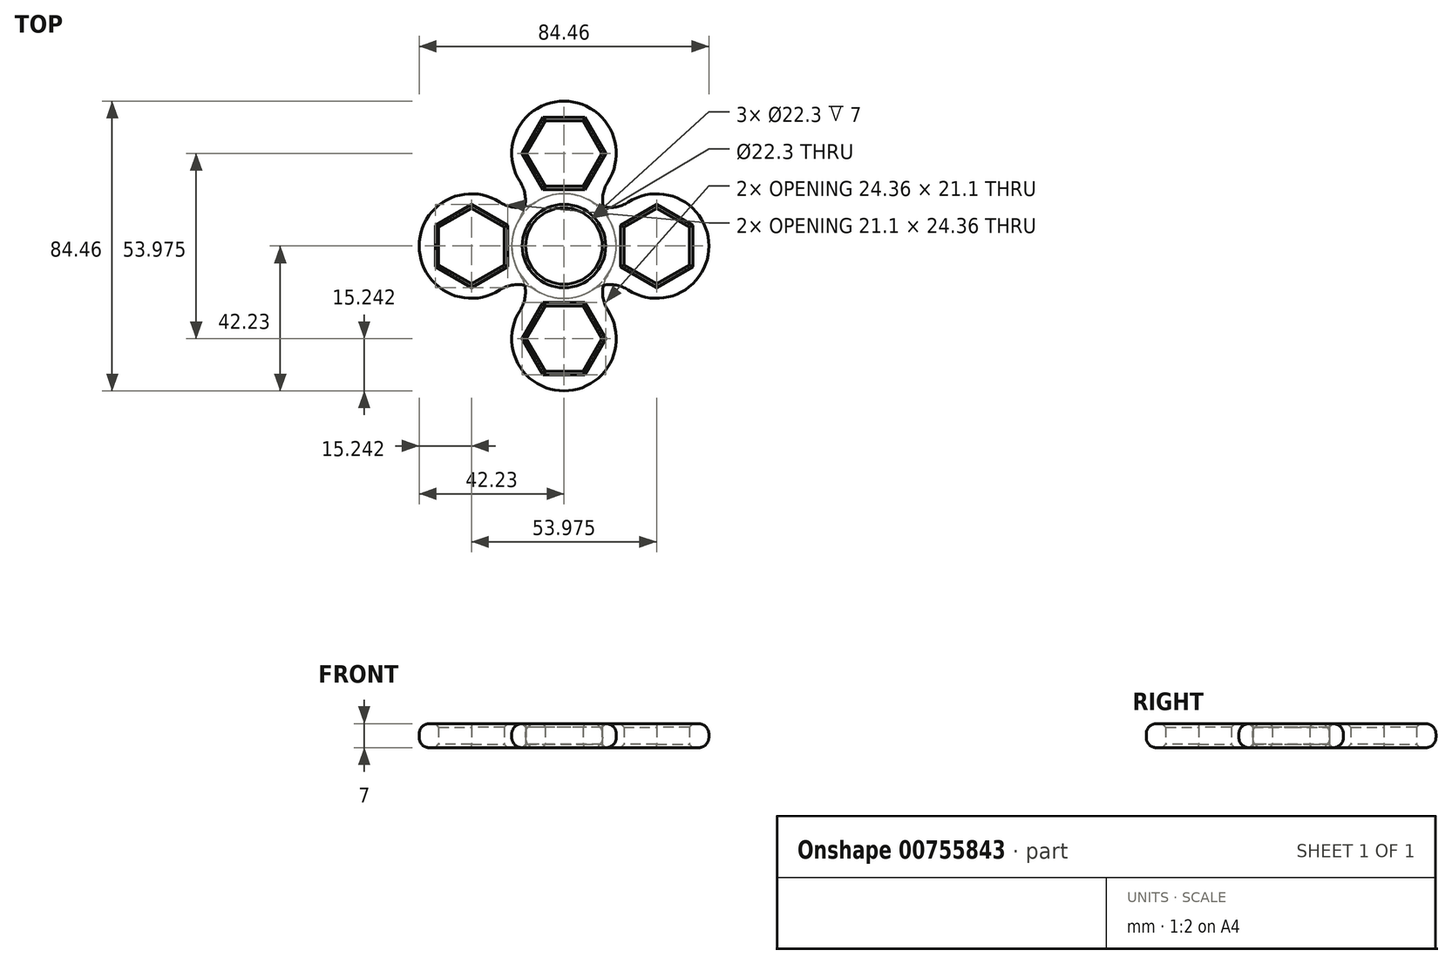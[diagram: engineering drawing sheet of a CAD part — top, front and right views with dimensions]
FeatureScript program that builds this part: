
annotation { "Feature Type Name" : "Feature", "Feature Type Description" : "" }
export const myFeature = defineFeature(function(context is Context, id is Id, definition is map)
    precondition{}
    {
        {
            var Q0;
            Q0=qCreatedBy(makeId("Top.planeOp"),FACE);
            var sketch = newSketch(context, id + "F0", { "sketchPlane" : qUnion([Q0])});
            skCircle(sketch, "E0", {"center": v(0, 0) * mm, "radius": 11.15 * mm});
            skCircle(sketch, "E1.cCircle", {"center": v(0, 26.99) * mm, "radius": 9.55 * mm, "construction": true});
            skLineSegment(sketch, "E1.0", {"start": v(5.51, 17.44) * mm, "end": v(-5.51, 17.44) * mm});
            skLineSegment(sketch, "E1.1", {"start": v(-5.51, 17.44) * mm, "end": v(-11.03, 26.99) * mm});
            skLineSegment(sketch, "E1.2", {"start": v(-11.03, 26.99) * mm, "end": v(-5.51, 36.54) * mm});
            skLineSegment(sketch, "E1.3", {"start": v(-5.51, 36.54) * mm, "end": v(5.51, 36.54) * mm});
            skLineSegment(sketch, "E1.4", {"start": v(5.51, 36.54) * mm, "end": v(11.03, 26.99) * mm});
            skLineSegment(sketch, "E1.5", {"start": v(11.03, 26.99) * mm, "end": v(5.51, 17.44) * mm});
            skPoint(sketch, "E1.0.midPoint", {"position": v(0, 17.44) * mm});
            skCircle(sketch, "E2", {"center": v(0, 26.99) * mm, "radius": 15.24 * mm});
            skCircle(sketch, "E3", {"center": v(0, 0) * mm, "radius": 15.24 * mm});
            skSolve(sketch);
        }
        {
            var Q0;
            {var subQ0=sQuery(id+"F0.wireOp",EDGE,"E1.1");Q0=makeQuery(id+"F0.imprint","IMPRINT",FACE,{"disambiguationData":[TD([[makeQuery(id+"F0.imprint","IMPRINT",EDGE,{"derivedFrom":subQ0}),1.0]])]});}
            var Q1;
            {var subQ1=sQuery(id+"F0.wireOp",EDGE,"E2");var subQ3=sQuery(id+"F0.wireOp",EDGE,"E0");var subQ9=makeQuery(id+"F0.imprint","INTERSECT",VERTEX,{"disambiguationData":[OD(0.0)],"derivedFrom":[subQ3,subQ1]});Q1=makeQuery(id+"F0.imprint","IMPRINT",FACE,{"disambiguationData":[TD([[makeQuery(id+"F0.imprint","IMPRINT",EDGE,{"disambiguationData":[TD([[subQ9,1.0]])],"derivedFrom":subQ3}),-1.0]])]});}
            var Q2;
            {var subQ0=sQuery(id+"F0.wireOp",EDGE,"E2");var subQ1=sQuery(id+"F0.wireOp",EDGE,"E0");var subQ2=makeQuery(id+"F0.imprint","INTERSECT",VERTEX,{"disambiguationData":[OD(0.0)],"derivedFrom":[subQ1,subQ0]});Q2=makeQuery(id+"F0.imprint","IMPRINT",FACE,{"disambiguationData":[TD([[makeQuery(id+"F0.imprint","IMPRINT",EDGE,{"disambiguationData":[TD([[subQ2,-1.0]])],"derivedFrom":subQ1}),-1.0]])]});}
            var Q3;
            {var subQ0=sQuery(id+"F0.wireOp",EDGE,"E3");var subQ1=sQuery(id+"F0.wireOp",EDGE,"E2");var subQ2=makeQuery(id+"F0.imprint","INTERSECT",VERTEX,{"disambiguationData":[OD(0.0)],"derivedFrom":[subQ1,subQ0]});Q3=makeQuery(id+"F0.imprint","IMPRINT",FACE,{"disambiguationData":[TD([[makeQuery(id+"F0.imprint","IMPRINT",EDGE,{"disambiguationData":[TD([[subQ2,-1.0]])],"derivedFrom":subQ1}),1.0]])]});}
            extrude(context, id + "F1", {"entities" : qUnion([Q0, Q1, Q2, Q3]), "depth" : 7 * mm, "offsetDistance" : 25.4 * mm});
        }
        {
            var Q0;
            {var subQ0=sQuery(id+"F0.wireOp",EDGE,"E3");var subQ1=sQuery(id+"F0.wireOp",EDGE,"E2");Q0=makeQuery(id+"F1.opExtrude","SWEPT_EDGE",EDGE,{"disambiguationData":[OSD([subQ1,subQ0]),TDD([makeQuery(id+"F0.imprint","INTERSECT",VERTEX,{"disambiguationData":[OD(0.0)],"derivedFrom":[subQ1,subQ0]})])]});}
            var Q1;
            {var subQ0=sQuery(id+"F0.wireOp",EDGE,"E3");var subQ1=sQuery(id+"F0.wireOp",EDGE,"E2");Q1=makeQuery(id+"F1.opExtrude","SWEPT_EDGE",EDGE,{"disambiguationData":[OSD([subQ1,subQ0]),TDD([makeQuery(id+"F0.imprint","INTERSECT",VERTEX,{"disambiguationData":[OD(1.0)],"derivedFrom":[subQ1,subQ0]})])]});}
            fillet(context, id + "F2", {"entities" : qUnion([Q0, Q1]), "radius" : 9.52 * mm, "tangentPropagation" : true, "allowEdgeOverflow" : false});
        }
        {
            var Q0;
            Q0=makeQuery(id+"F1.opExtrude","SWEPT_BODY",BODY,{"disambiguationData":[OSD([sQuery(id+"F0.wireOp",EDGE,"E0"),sQuery(id+"F0.wireOp",EDGE,"d1f96c89-ae24-44dc-95b8-3d53eee9b90a.0"),sQuery(id+"F0.wireOp",EDGE,"E1.0"),sQuery(id+"F0.wireOp",EDGE,"E1.1"),sQuery(id+"F0.wireOp",EDGE,"E1.2"),sQuery(id+"F0.wireOp",EDGE,"E1.3"),sQuery(id+"F0.wireOp",EDGE,"E1.4"),sQuery(id+"F0.wireOp",EDGE,"E1.5"),sQuery(id+"F0.wireOp",EDGE,"6467eb64-f5fc-4fa4-b67a-5fdd80484858.0"),sQuery(id+"F0.wireOp",EDGE,"6467eb64-f5fc-4fa4-b67a-5fdd80484858.2"),sQuery(id+"F0.wireOp",EDGE,"6467eb64-f5fc-4fa4-b67a-5fdd80484858.3"),sQuery(id+"F0.wireOp",EDGE,"6467eb64-f5fc-4fa4-b67a-5fdd80484858.4"),sQuery(id+"F0.wireOp",EDGE,"6467eb64-f5fc-4fa4-b67a-5fdd80484858.5"),sQuery(id+"F0.wireOp",EDGE,"e1e534cc-2f33-4b0f-82cc-b4de4e4070e7"),sQuery(id+"F0.wireOp",EDGE,"d04765f5-1735-495e-b364-6d969f9b3d5d"),sQuery(id+"F0.wireOp",EDGE,"77a682f6-1ae9-43b9-b4da-7f019d4a444a.0"),sQuery(id+"F0.wireOp",EDGE,"27ab2300-1543-4c0a-a06e-bdf80a921956.0"),sQuery(id+"F0.wireOp",EDGE,"7b8874fc-19ec-4d05-a443-a3cdac1f19cd.filletArc"),sQuery(id+"F0.wireOp",EDGE,"lxG7lnsp-9xvN-WL6z-RJoO-r6IwSvIQtlOm"),sQuery(id+"F0.wireOp",EDGE,"8nAJOfJ4-Ij3l-DfIw-Xt9b-HZkO6DjjanfU")])]});
            var Q1;
            Q1=makeQuery(id+"F1.opExtrude","SWEPT_FACE",FACE,{"disambiguationData":[OSD([sQuery(id+"F0.wireOp",EDGE,"E0")])]});
            circularPattern(context, id + "F3", {"entities" : qUnion([Q0]), "axis" : qUnion([Q1]), "angle" : 360 * degree, "instanceCount" : 4, "oppositeDirection" : true, "equalSpace" : true});
        }
        {
            var Q0;
            Q0=makeQuery(id+"F1.opExtrude","SWEPT_FACE",FACE,{"disambiguationData":[OSD([sQuery(id+"F0.wireOp",EDGE,"E0")])]});
            var Q1;
            Q1=makeQuery(id+"F3.opPattern","COPY",EDGE,{"derivedFrom":makeQuery(id+"F1.opExtrude","CAP_EDGE",EDGE,{"disambiguationData":[OSD([sQuery(id+"F0.wireOp",EDGE,"E1.3")])],"isStart":true}),"instanceName":"1"});
            var Q2;
            Q2=makeQuery(id+"F3.opPattern","COPY",EDGE,{"derivedFrom":makeQuery(id+"F1.opExtrude","CAP_EDGE",EDGE,{"disambiguationData":[OSD([sQuery(id+"F0.wireOp",EDGE,"E1.3")])],"isStart":false}),"instanceName":"1"});
            var Q3;
            Q3=makeQuery(id+"F3.opPattern","COPY",EDGE,{"derivedFrom":makeQuery(id+"F1.opExtrude","CAP_EDGE",EDGE,{"disambiguationData":[OSD([sQuery(id+"F0.wireOp",EDGE,"E1.2")])],"isStart":false}),"instanceName":"1"});
            var Q4;
            Q4=makeQuery(id+"F3.opPattern","COPY",EDGE,{"derivedFrom":makeQuery(id+"F1.opExtrude","CAP_EDGE",EDGE,{"disambiguationData":[OSD([sQuery(id+"F0.wireOp",EDGE,"E1.2")])],"isStart":true}),"instanceName":"1"});
            var Q5;
            Q5=makeQuery(id+"F3.opPattern","COPY",EDGE,{"derivedFrom":makeQuery(id+"F1.opExtrude","CAP_EDGE",EDGE,{"disambiguationData":[OSD([sQuery(id+"F0.wireOp",EDGE,"E1.1")])],"isStart":false}),"instanceName":"1"});
            var Q6;
            Q6=makeQuery(id+"F3.opPattern","COPY",EDGE,{"derivedFrom":makeQuery(id+"F1.opExtrude","CAP_EDGE",EDGE,{"disambiguationData":[OSD([sQuery(id+"F0.wireOp",EDGE,"E1.0")])],"isStart":false}),"instanceName":"1"});
            var Q7;
            Q7=makeQuery(id+"F3.opPattern","COPY",EDGE,{"derivedFrom":makeQuery(id+"F1.opExtrude","CAP_EDGE",EDGE,{"disambiguationData":[OSD([sQuery(id+"F0.wireOp",EDGE,"E1.5")])],"isStart":false}),"instanceName":"1"});
            var Q8;
            Q8=makeQuery(id+"F3.opPattern","COPY",EDGE,{"derivedFrom":makeQuery(id+"F1.opExtrude","CAP_EDGE",EDGE,{"disambiguationData":[OSD([sQuery(id+"F0.wireOp",EDGE,"E1.4")])],"isStart":true}),"instanceName":"1"});
            var Q9;
            Q9=makeQuery(id+"F3.opPattern","COPY",EDGE,{"derivedFrom":makeQuery(id+"F1.opExtrude","CAP_EDGE",EDGE,{"disambiguationData":[OSD([sQuery(id+"F0.wireOp",EDGE,"E1.4")])],"isStart":false}),"instanceName":"1"});
            var Q10;
            Q10=makeQuery(id+"F1.opExtrude","CAP_EDGE",EDGE,{"disambiguationData":[OSD([sQuery(id+"F0.wireOp",EDGE,"E1.1")])],"isStart":false});
            var Q11;
            Q11=makeQuery(id+"F1.opExtrude","CAP_EDGE",EDGE,{"disambiguationData":[OSD([sQuery(id+"F0.wireOp",EDGE,"E1.1")])],"isStart":true});
            var Q12;
            Q12=makeQuery(id+"F1.opExtrude","CAP_EDGE",EDGE,{"disambiguationData":[OSD([sQuery(id+"F0.wireOp",EDGE,"E1.0")])],"isStart":true});
            var Q13;
            Q13=makeQuery(id+"F1.opExtrude","CAP_EDGE",EDGE,{"disambiguationData":[OSD([sQuery(id+"F0.wireOp",EDGE,"E1.0")])],"isStart":false});
            var Q14;
            Q14=makeQuery(id+"F1.opExtrude","CAP_EDGE",EDGE,{"disambiguationData":[OSD([sQuery(id+"F0.wireOp",EDGE,"E1.5")])],"isStart":false});
            var Q15;
            Q15=makeQuery(id+"F1.opExtrude","CAP_EDGE",EDGE,{"disambiguationData":[OSD([sQuery(id+"F0.wireOp",EDGE,"E1.5")])],"isStart":true});
            var Q16;
            Q16=makeQuery(id+"F1.opExtrude","CAP_EDGE",EDGE,{"disambiguationData":[OSD([sQuery(id+"F0.wireOp",EDGE,"E1.4")])],"isStart":false});
            var Q17;
            Q17=makeQuery(id+"F1.opExtrude","CAP_EDGE",EDGE,{"disambiguationData":[OSD([sQuery(id+"F0.wireOp",EDGE,"E1.3")])],"isStart":false});
            var Q18;
            Q18=makeQuery(id+"F1.opExtrude","CAP_EDGE",EDGE,{"disambiguationData":[OSD([sQuery(id+"F0.wireOp",EDGE,"E1.2")])],"isStart":false});
            var Q19;
            Q19=makeQuery(id+"F1.opExtrude","CAP_EDGE",EDGE,{"disambiguationData":[OSD([sQuery(id+"F0.wireOp",EDGE,"E1.3")])],"isStart":true});
            var Q20;
            Q20=makeQuery(id+"F1.opExtrude","CAP_EDGE",EDGE,{"disambiguationData":[OSD([sQuery(id+"F0.wireOp",EDGE,"E1.4")])],"isStart":true});
            var Q21;
            Q21=makeQuery(id+"F1.opExtrude","CAP_EDGE",EDGE,{"disambiguationData":[OSD([sQuery(id+"F0.wireOp",EDGE,"E1.2")])],"isStart":true});
            var Q22;
            Q22=makeQuery(id+"F3.opPattern","COPY",EDGE,{"derivedFrom":makeQuery(id+"F1.opExtrude","CAP_EDGE",EDGE,{"disambiguationData":[OSD([sQuery(id+"F0.wireOp",EDGE,"E1.5")])],"isStart":true}),"instanceName":"1"});
            var Q23;
            Q23=makeQuery(id+"F3.opPattern","COPY",EDGE,{"derivedFrom":makeQuery(id+"F1.opExtrude","CAP_EDGE",EDGE,{"disambiguationData":[OSD([sQuery(id+"F0.wireOp",EDGE,"E1.0")])],"isStart":true}),"instanceName":"1"});
            var Q24;
            Q24=makeQuery(id+"F3.opPattern","COPY",EDGE,{"derivedFrom":makeQuery(id+"F1.opExtrude","CAP_EDGE",EDGE,{"disambiguationData":[OSD([sQuery(id+"F0.wireOp",EDGE,"E1.1")])],"isStart":true}),"instanceName":"1"});
            var Q25;
            Q25=makeQuery(id+"F3.opPattern","COPY",EDGE,{"derivedFrom":makeQuery(id+"F1.opExtrude","CAP_EDGE",EDGE,{"disambiguationData":[OSD([sQuery(id+"F0.wireOp",EDGE,"E1.5")])],"isStart":false}),"instanceName":"2"});
            var Q26;
            Q26=makeQuery(id+"F3.opPattern","COPY",EDGE,{"derivedFrom":makeQuery(id+"F1.opExtrude","CAP_EDGE",EDGE,{"disambiguationData":[OSD([sQuery(id+"F0.wireOp",EDGE,"E1.5")])],"isStart":true}),"instanceName":"2"});
            var Q27;
            Q27=makeQuery(id+"F3.opPattern","COPY",EDGE,{"derivedFrom":makeQuery(id+"F1.opExtrude","CAP_EDGE",EDGE,{"disambiguationData":[OSD([sQuery(id+"F0.wireOp",EDGE,"E1.0")])],"isStart":false}),"instanceName":"2"});
            var Q28;
            Q28=makeQuery(id+"F3.opPattern","COPY",EDGE,{"derivedFrom":makeQuery(id+"F1.opExtrude","CAP_EDGE",EDGE,{"disambiguationData":[OSD([sQuery(id+"F0.wireOp",EDGE,"E1.0")])],"isStart":true}),"instanceName":"2"});
            var Q29;
            Q29=makeQuery(id+"F3.opPattern","COPY",EDGE,{"derivedFrom":makeQuery(id+"F1.opExtrude","CAP_EDGE",EDGE,{"disambiguationData":[OSD([sQuery(id+"F0.wireOp",EDGE,"E1.4")])],"isStart":false}),"instanceName":"2"});
            var Q30;
            Q30=makeQuery(id+"F3.opPattern","COPY",EDGE,{"derivedFrom":makeQuery(id+"F1.opExtrude","CAP_EDGE",EDGE,{"disambiguationData":[OSD([sQuery(id+"F0.wireOp",EDGE,"E1.4")])],"isStart":true}),"instanceName":"2"});
            var Q31;
            Q31=makeQuery(id+"F3.opPattern","COPY",EDGE,{"derivedFrom":makeQuery(id+"F1.opExtrude","CAP_EDGE",EDGE,{"disambiguationData":[OSD([sQuery(id+"F0.wireOp",EDGE,"E1.3")])],"isStart":true}),"instanceName":"2"});
            var Q32;
            Q32=makeQuery(id+"F3.opPattern","COPY",EDGE,{"derivedFrom":makeQuery(id+"F1.opExtrude","CAP_EDGE",EDGE,{"disambiguationData":[OSD([sQuery(id+"F0.wireOp",EDGE,"E1.2")])],"isStart":true}),"instanceName":"2"});
            var Q33;
            Q33=makeQuery(id+"F3.opPattern","COPY",EDGE,{"derivedFrom":makeQuery(id+"F1.opExtrude","CAP_EDGE",EDGE,{"disambiguationData":[OSD([sQuery(id+"F0.wireOp",EDGE,"E1.1")])],"isStart":true}),"instanceName":"2"});
            var Q34;
            Q34=makeQuery(id+"F3.opPattern","COPY",EDGE,{"derivedFrom":makeQuery(id+"F1.opExtrude","CAP_EDGE",EDGE,{"disambiguationData":[OSD([sQuery(id+"F0.wireOp",EDGE,"E1.2")])],"isStart":false}),"instanceName":"2"});
            var Q35;
            Q35=makeQuery(id+"F3.opPattern","COPY",EDGE,{"derivedFrom":makeQuery(id+"F1.opExtrude","CAP_EDGE",EDGE,{"disambiguationData":[OSD([sQuery(id+"F0.wireOp",EDGE,"E1.1")])],"isStart":false}),"instanceName":"2"});
            var Q36;
            Q36=makeQuery(id+"F3.opPattern","COPY",EDGE,{"derivedFrom":makeQuery(id+"F1.opExtrude","CAP_EDGE",EDGE,{"disambiguationData":[OSD([sQuery(id+"F0.wireOp",EDGE,"E1.3")])],"isStart":false}),"instanceName":"2"});
            var Q37;
            Q37=makeQuery(id+"F3.opPattern","COPY",EDGE,{"derivedFrom":makeQuery(id+"F1.opExtrude","CAP_EDGE",EDGE,{"disambiguationData":[OSD([sQuery(id+"F0.wireOp",EDGE,"E1.5")])],"isStart":false}),"instanceName":"3"});
            var Q38;
            Q38=makeQuery(id+"F3.opPattern","COPY",EDGE,{"derivedFrom":makeQuery(id+"F1.opExtrude","CAP_EDGE",EDGE,{"disambiguationData":[OSD([sQuery(id+"F0.wireOp",EDGE,"E1.4")])],"isStart":false}),"instanceName":"3"});
            var Q39;
            Q39=makeQuery(id+"F3.opPattern","COPY",EDGE,{"derivedFrom":makeQuery(id+"F1.opExtrude","CAP_EDGE",EDGE,{"disambiguationData":[OSD([sQuery(id+"F0.wireOp",EDGE,"E1.3")])],"isStart":false}),"instanceName":"3"});
            var Q40;
            Q40=makeQuery(id+"F3.opPattern","COPY",EDGE,{"derivedFrom":makeQuery(id+"F1.opExtrude","CAP_EDGE",EDGE,{"disambiguationData":[OSD([sQuery(id+"F0.wireOp",EDGE,"E1.2")])],"isStart":false}),"instanceName":"3"});
            var Q41;
            Q41=makeQuery(id+"F3.opPattern","COPY",EDGE,{"derivedFrom":makeQuery(id+"F1.opExtrude","CAP_EDGE",EDGE,{"disambiguationData":[OSD([sQuery(id+"F0.wireOp",EDGE,"E1.1")])],"isStart":false}),"instanceName":"3"});
            var Q42;
            Q42=makeQuery(id+"F3.opPattern","COPY",EDGE,{"derivedFrom":makeQuery(id+"F1.opExtrude","CAP_EDGE",EDGE,{"disambiguationData":[OSD([sQuery(id+"F0.wireOp",EDGE,"E1.0")])],"isStart":false}),"instanceName":"3"});
            var Q43;
            Q43=makeQuery(id+"F3.opPattern","COPY",EDGE,{"derivedFrom":makeQuery(id+"F1.opExtrude","CAP_EDGE",EDGE,{"disambiguationData":[OSD([sQuery(id+"F0.wireOp",EDGE,"E1.5")])],"isStart":true}),"instanceName":"3"});
            var Q44;
            Q44=makeQuery(id+"F3.opPattern","COPY",EDGE,{"derivedFrom":makeQuery(id+"F1.opExtrude","CAP_EDGE",EDGE,{"disambiguationData":[OSD([sQuery(id+"F0.wireOp",EDGE,"E1.4")])],"isStart":true}),"instanceName":"3"});
            var Q45;
            Q45=makeQuery(id+"F3.opPattern","COPY",EDGE,{"derivedFrom":makeQuery(id+"F1.opExtrude","CAP_EDGE",EDGE,{"disambiguationData":[OSD([sQuery(id+"F0.wireOp",EDGE,"E1.3")])],"isStart":true}),"instanceName":"3"});
            var Q46;
            Q46=makeQuery(id+"F3.opPattern","COPY",EDGE,{"derivedFrom":makeQuery(id+"F1.opExtrude","CAP_EDGE",EDGE,{"disambiguationData":[OSD([sQuery(id+"F0.wireOp",EDGE,"E1.2")])],"isStart":true}),"instanceName":"3"});
            var Q47;
            Q47=makeQuery(id+"F3.opPattern","COPY",EDGE,{"derivedFrom":makeQuery(id+"F1.opExtrude","CAP_EDGE",EDGE,{"disambiguationData":[OSD([sQuery(id+"F0.wireOp",EDGE,"E1.1")])],"isStart":true}),"instanceName":"3"});
            var Q48;
            Q48=makeQuery(id+"F3.opPattern","COPY",EDGE,{"derivedFrom":makeQuery(id+"F1.opExtrude","CAP_EDGE",EDGE,{"disambiguationData":[OSD([sQuery(id+"F0.wireOp",EDGE,"E1.0")])],"isStart":true}),"instanceName":"3"});
            chamfer(context, id + "F4", {"entities" : qUnion([Q0, Q1, Q2, Q3, Q4, Q5, Q6, Q7, Q8, Q9, Q10, Q11, Q12, Q13, Q14, Q15, Q16, Q17, Q18, Q19, Q20, Q21, Q22, Q23, Q24, Q25, Q26, Q27, Q28, Q29, Q30, Q31, Q32, Q33, Q34, Q35, Q36, Q37, Q38, Q39, Q40, Q41, Q42, Q43, Q44, Q45, Q46, Q47, Q48]), "width" : 1 * mm, "tangentPropagation" : true});
        }
        {
            var Q0;
            Q0=makeQuery(id+"F1.opExtrude","CAP_EDGE",EDGE,{"disambiguationData":[OSD([sQuery(id+"F0.wireOp",EDGE,"E2")])],"isStart":false});
            var Q1;
            Q1=makeQuery(id+"F1.opExtrude","CAP_EDGE",EDGE,{"disambiguationData":[OSD([sQuery(id+"F0.wireOp",EDGE,"E2")])],"isStart":true});
            var Q2;
            Q2=makeQuery(id+"F3.opPattern","COPY",EDGE,{"derivedFrom":makeQuery(id+"F1.opExtrude","CAP_EDGE",EDGE,{"disambiguationData":[OSD([sQuery(id+"F0.wireOp",EDGE,"E2")])],"isStart":true}),"instanceName":"1"});
            var Q3;
            Q3=makeQuery(id+"F3.opPattern","COPY",EDGE,{"derivedFrom":makeQuery(id+"F1.opExtrude","CAP_EDGE",EDGE,{"disambiguationData":[OSD([sQuery(id+"F0.wireOp",EDGE,"E2")])],"isStart":false}),"instanceName":"1"});
            var Q4;
            Q4=makeQuery(id+"F3.opPattern","COPY",EDGE,{"derivedFrom":makeQuery(id+"F1.opExtrude","CAP_EDGE",EDGE,{"disambiguationData":[OSD([sQuery(id+"F0.wireOp",EDGE,"E2")])],"isStart":true}),"instanceName":"2"});
            var Q5;
            Q5=makeQuery(id+"F3.opPattern","COPY",EDGE,{"derivedFrom":makeQuery(id+"F1.opExtrude","CAP_EDGE",EDGE,{"disambiguationData":[OSD([sQuery(id+"F0.wireOp",EDGE,"E2")])],"isStart":false}),"instanceName":"2"});
            var Q6;
            Q6=makeQuery(id+"F3.opPattern","COPY",EDGE,{"derivedFrom":makeQuery(id+"F1.opExtrude","CAP_EDGE",EDGE,{"disambiguationData":[OSD([sQuery(id+"F0.wireOp",EDGE,"E2")])],"isStart":false}),"instanceName":"3"});
            var Q7;
            Q7=makeQuery(id+"F3.opPattern","COPY",EDGE,{"derivedFrom":makeQuery(id+"F1.opExtrude","CAP_EDGE",EDGE,{"disambiguationData":[OSD([sQuery(id+"F0.wireOp",EDGE,"E2")])],"isStart":true}),"instanceName":"3"});
            fillet(context, id + "F5", {"entities" : qUnion([Q0, Q1, Q2, Q3, Q4, Q5, Q6, Q7]), "radius" : 3 * mm, "tangentPropagation" : true, "allowEdgeOverflow" : false});
        }
    });
